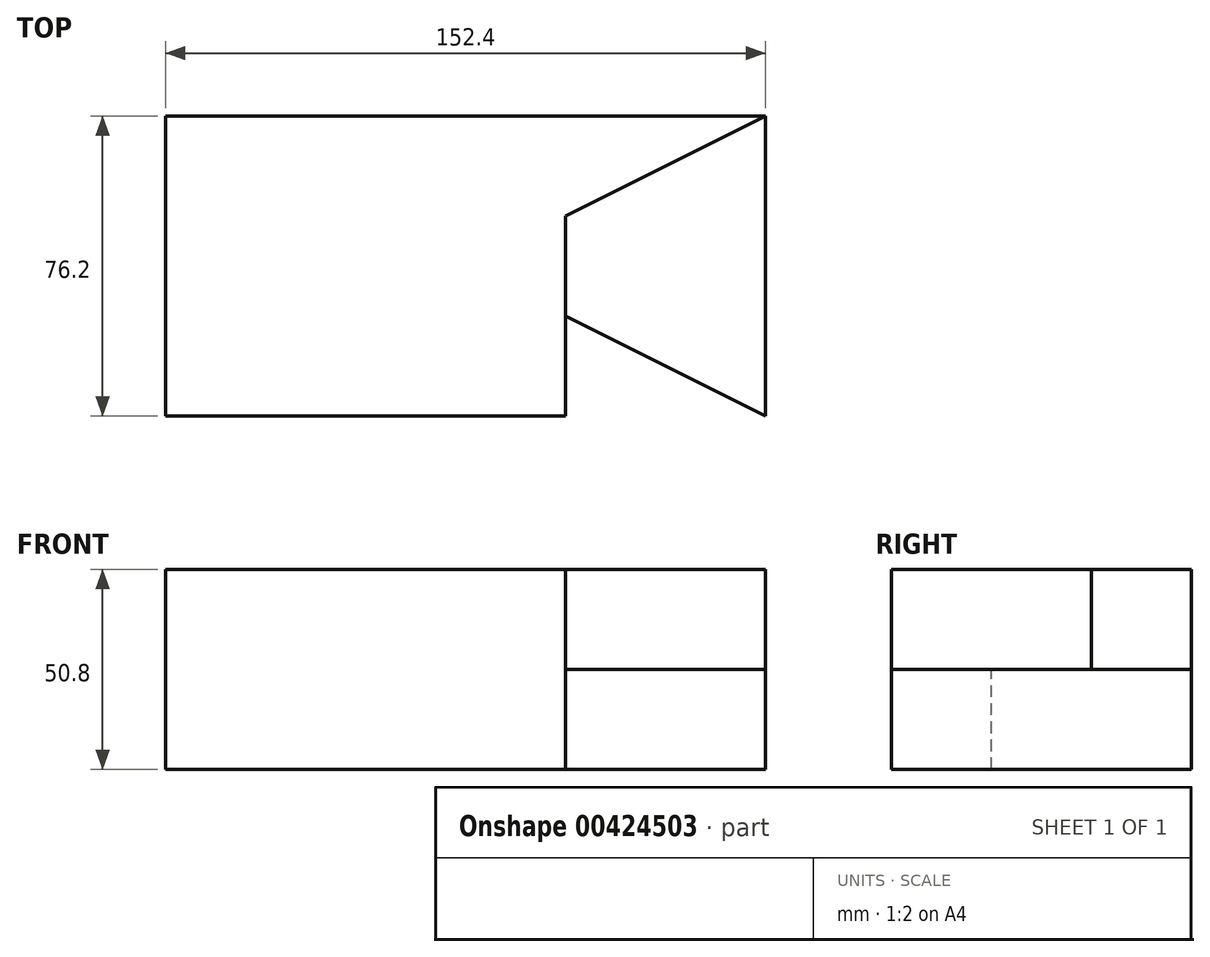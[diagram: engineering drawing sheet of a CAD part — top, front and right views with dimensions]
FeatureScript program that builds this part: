
annotation { "Feature Type Name" : "Feature", "Feature Type Description" : "" }
export const myFeature = defineFeature(function(context is Context, id is Id, definition is map)
    precondition{}
    {
        {
            var Q0;
            Q0=qCreatedBy(makeId("Front.planeOp"),FACE);
            var sketch = newSketch(context, id + "F0", { "sketchPlane" : qUnion([Q0])});
            skLineSegment(sketch, "E0", {"start": v(0, 0) * mm, "end": v(152.4, 0) * mm});
            skLineSegment(sketch, "E1", {"start": v(0, 0) * mm, "end": v(0, 50.8) * mm});
            skLineSegment(sketch, "E2", {"start": v(0, 50.8) * mm, "end": v(152.4, 50.8) * mm});
            skLineSegment(sketch, "E3", {"start": v(152.4, 0) * mm, "end": v(152.4, 50.8) * mm});
            skSolve(sketch);
        }
        {
            var Q0;
            Q0=makeQuery(id+"F0.imprint","IMPRINT",FACE,{"disambiguationData":[TD([[makeQuery(id+"F0.imprint","IMPRINT",EDGE,{"derivedFrom":sQuery(id+"F0.wireOp",EDGE,"E0")}),1.0]])]});
            extrude(context, id + "F1", {"entities" : qUnion([Q0]), "oppositeDirection" : true, "depth" : 76.2 * mm});
        }
        {
            var Q0;
            Q0=makeQuery(id+"F1.opExtrude","SWEPT_FACE",FACE,{"disambiguationData":[OSD([sQuery(id+"F0.wireOp",EDGE,"E2")])]});
            var sketch = newSketch(context, id + "F2", { "sketchPlane" : qUnion([Q0])});
            skLineSegment(sketch, "E4", {"start": v(0, 0) * mm, "end": v(101.6, 0) * mm});
            skLineSegment(sketch, "E5", {"start": v(101.6, 0) * mm, "end": v(101.6, 76.2) * mm});
            skLineSegment(sketch, "E6", {"start": v(101.6, 76.2) * mm, "end": v(0, 76.2) * mm});
            skLineSegment(sketch, "E7", {"start": v(0, 76.2) * mm, "end": v(0, 0) * mm});
            skLineSegment(sketch, "E8", {"start": v(101.6, 0) * mm, "end": v(101.6, 25.4) * mm});
            skLineSegment(sketch, "E9", {"start": v(101.6, 25.4) * mm, "end": v(152.4, 0) * mm});
            skLineSegment(sketch, "E10", {"start": v(101.6, 0) * mm, "end": v(152.4, 0) * mm});
            skLineSegment(sketch, "E11", {"start": v(101.6, 76.2) * mm, "end": v(101.6, 50.8) * mm});
            skLineSegment(sketch, "E12", {"start": v(101.6, 25.4) * mm, "end": v(101.6, 0) * mm});
            skLineSegment(sketch, "E13", {"start": v(101.6, 50.8) * mm, "end": v(152.4, 76.2) * mm});
            skLineSegment(sketch, "E14", {"start": v(101.6, 76.2) * mm, "end": v(152.4, 76.2) * mm});
            skLineSegment(sketch, "E15", {"start": v(152.4, 76.2) * mm, "end": v(152.4, 0) * mm});
            skLineSegment(sketch, "E16", {"start": v(101.6, 50.8) * mm, "end": v(101.6, 25.4) * mm});
            skSolve(sketch);
        }
        {
            var Q0;
            Q0=makeQuery(id+"F2.imprint","IMPRINT",FACE,{"disambiguationData":[TD([[makeQuery(id+"F2.imprint","IMPRINT",EDGE,{"derivedFrom":sQuery(id+"F2.wireOp",EDGE,"E9")}),-1.0]])]});
            var Q1;
            Q1=makeQuery(id+"F2.imprint","IMPRINT",FACE,{"disambiguationData":[TD([[makeQuery(id+"F2.imprint","IMPRINT",EDGE,{"derivedFrom":sQuery(id+"F2.wireOp",EDGE,"E11")}),1.0]])]});
            extrude(context, id + "F3", {"entities" : qUnion([Q0, Q1]), "operationType" : NewBodyOperationType.REMOVE, "oppositeDirection" : true, "depth" : 50.8 * mm});
        }
        {
            var Q0;
            Q0=makeQuery(id+"F1.opExtrude","SWEPT_FACE",FACE,{"disambiguationData":[OSD([sQuery(id+"F0.wireOp",EDGE,"E2")])]});
            var sketch = newSketch(context, id + "F4", { "sketchPlane" : qUnion([Q0])});
            skLineSegment(sketch, "E17", {"start": v(101.6, 50.8) * mm, "end": v(101.6, 25.4) * mm});
            skLineSegment(sketch, "E18", {"start": v(101.6, 50.8) * mm, "end": v(152.4, 76.2) * mm});
            skLineSegment(sketch, "E19", {"start": v(101.6, 25.4) * mm, "end": v(152.4, 0) * mm});
            skLineSegment(sketch, "E20", {"start": v(152.4, 0) * mm, "end": v(152.4, 76.2) * mm});
            skSolve(sketch);
        }
        {
            var Q0;
            Q0=makeQuery(id+"F4.imprint","IMPRINT",FACE,{"disambiguationData":[TD([[makeQuery(id+"F4.imprint","IMPRINT",EDGE,{"derivedFrom":sQuery(id+"F4.wireOp",EDGE,"E17")}),1.0]])]});
            extrude(context, id + "F5", {"entities" : qUnion([Q0]), "operationType" : NewBodyOperationType.REMOVE, "oppositeDirection" : true, "depth" : 25.4 * mm});
        }
    });
